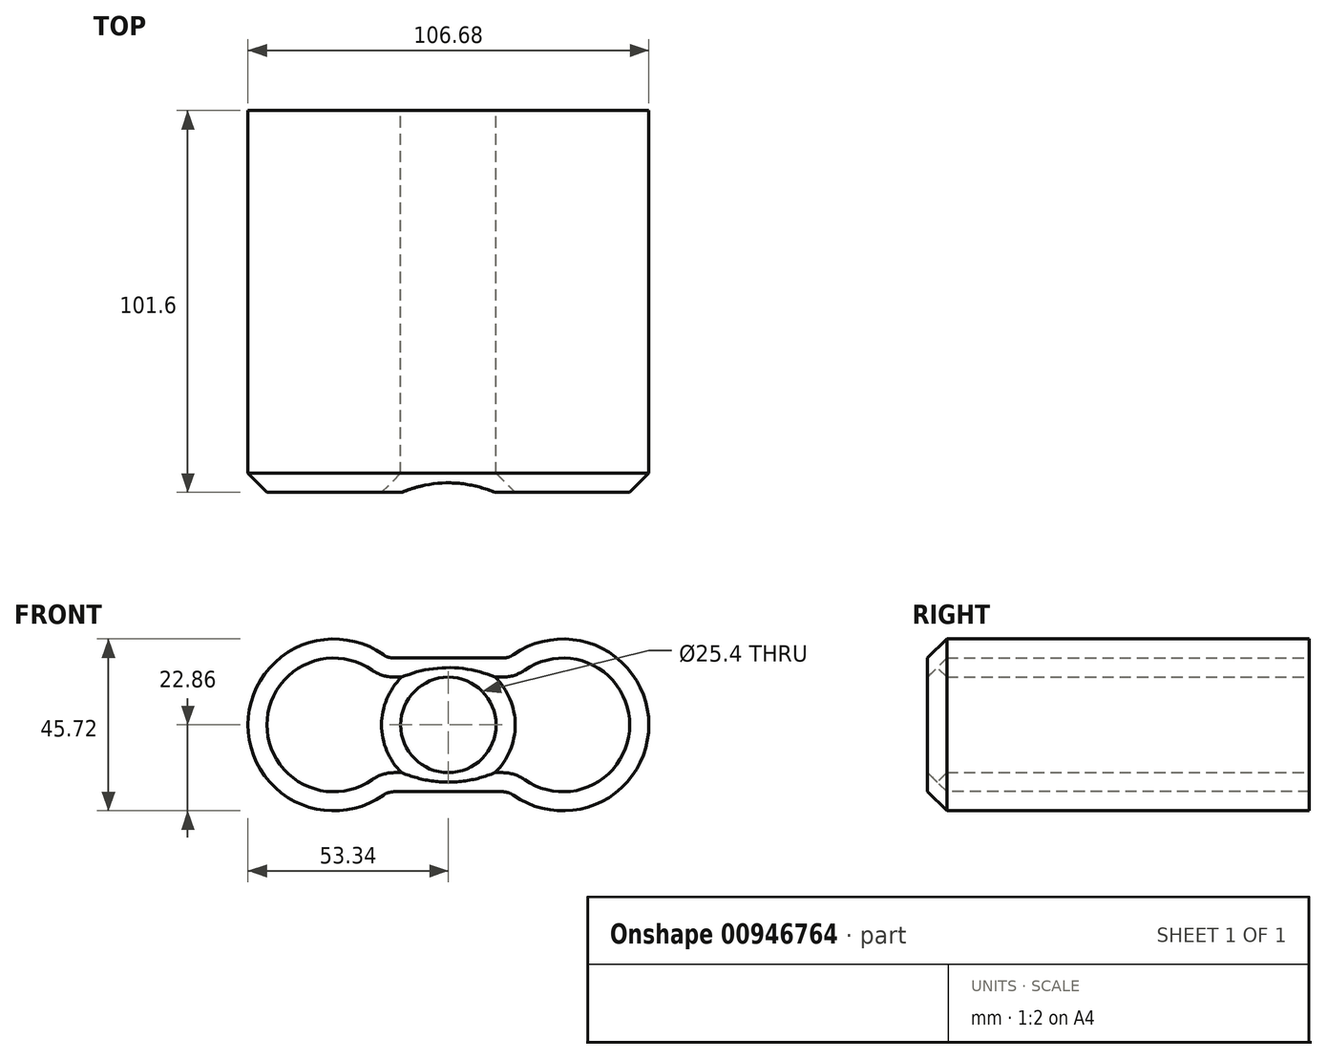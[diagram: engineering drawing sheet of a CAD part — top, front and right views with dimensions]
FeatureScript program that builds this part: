
annotation { "Feature Type Name" : "Feature", "Feature Type Description" : "" }
export const myFeature = defineFeature(function(context is Context, id is Id, definition is map)
    precondition{}
    {
        {
            var Q0;
            Q0=qCreatedBy(makeId("Front.planeOp"),FACE);
            var sketch = newSketch(context, id + "F0", { "sketchPlane" : qUnion([Q0])});
            skLineSegment(sketch, "E0", {"start": v(-30.48, 0) * mm, "end": v(30.48, 0) * mm});
            skArc(sketch, "E1", {"start": v(-16.11, 17.78) * mm, "mid": v(-53.34, 0) * mm, "end": v(-16.11, -17.78) * mm});
            skArc(sketch, "E2", {"start": v(16.11, -17.78) * mm, "mid": v(53.34, 0) * mm, "end": v(16.11, 17.78) * mm});
            skLineSegment(sketch, "E3", {"start": v(-16.11, 17.78) * mm, "end": v(16.11, 17.78) * mm});
            skLineSegment(sketch, "E4", {"start": v(-16.11, -17.78) * mm, "end": v(16.11, -17.78) * mm});
            skCircle(sketch, "E5", {"center": v(0, 0) * mm, "radius": 7.62 * mm});
            skCircle(sketch, "E6", {"center": v(0, 0) * mm, "radius": 12.7 * mm});
            skSolve(sketch);
        }
        {
            var Q0;
            Q0=makeQuery(id+"F0.imprint","IMPRINT",FACE,{"disambiguationData":[TD([[makeQuery(id+"F0.imprint","IMPRINT",EDGE,{"derivedFrom":sQuery(id+"F0.wireOp",EDGE,"E1")}),1.0]])]});
            extrude(context, id + "F1", {"entities" : qUnion([Q0]), "depth" : 101.6 * mm, "offsetDistance" : 25.4 * mm});
        }
        {
            var Q0;
            Q0=makeQuery(id+"F1.opExtrude","SWEPT_EDGE",EDGE,{"disambiguationData":[OSD([sQuery(id+"F0.wireOp",EDGE,"E1"),sQuery(id+"F0.wireOp",EDGE,"E3")])]});
            var Q1;
            Q1=makeQuery(id+"F1.opExtrude","SWEPT_EDGE",EDGE,{"disambiguationData":[OSD([sQuery(id+"F0.wireOp",EDGE,"E2"),sQuery(id+"F0.wireOp",EDGE,"E3")])]});
            fillet(context, id + "F2", {"entities" : qUnion([Q0, Q1]), "radius" : 5.08 * mm, "tangentPropagation" : true, "allowEdgeOverflow" : false});
        }
        {
            var Q0;
            Q0=makeQuery(id+"F1.opExtrude","SWEPT_EDGE",EDGE,{"disambiguationData":[OSD([sQuery(id+"F0.wireOp",EDGE,"E1"),sQuery(id+"F0.wireOp",EDGE,"E4")])]});
            var Q1;
            Q1=makeQuery(id+"F1.opExtrude","SWEPT_EDGE",EDGE,{"disambiguationData":[OSD([sQuery(id+"F0.wireOp",EDGE,"E2"),sQuery(id+"F0.wireOp",EDGE,"E4")])]});
            fillet(context, id + "F3", {"entities" : qUnion([Q0, Q1]), "radius" : 5.08 * mm, "tangentPropagation" : true, "allowEdgeOverflow" : false});
        }
        {
            var Q0;
            Q0=makeQuery(id+"F1.opExtrude","CAP_FACE",FACE,{"disambiguationData":[OSD([sQuery(id+"F0.wireOp",EDGE,"E1"),sQuery(id+"F0.wireOp",EDGE,"E2"),sQuery(id+"F0.wireOp",EDGE,"E3"),sQuery(id+"F0.wireOp",EDGE,"E4"),sQuery(id+"F0.wireOp",EDGE,"E6")])],"isStart":false});
            chamfer(context, id + "F4", {"entities" : qUnion([Q0]), "width" : 5.08 * mm, "tangentPropagation" : true});
        }
    });
